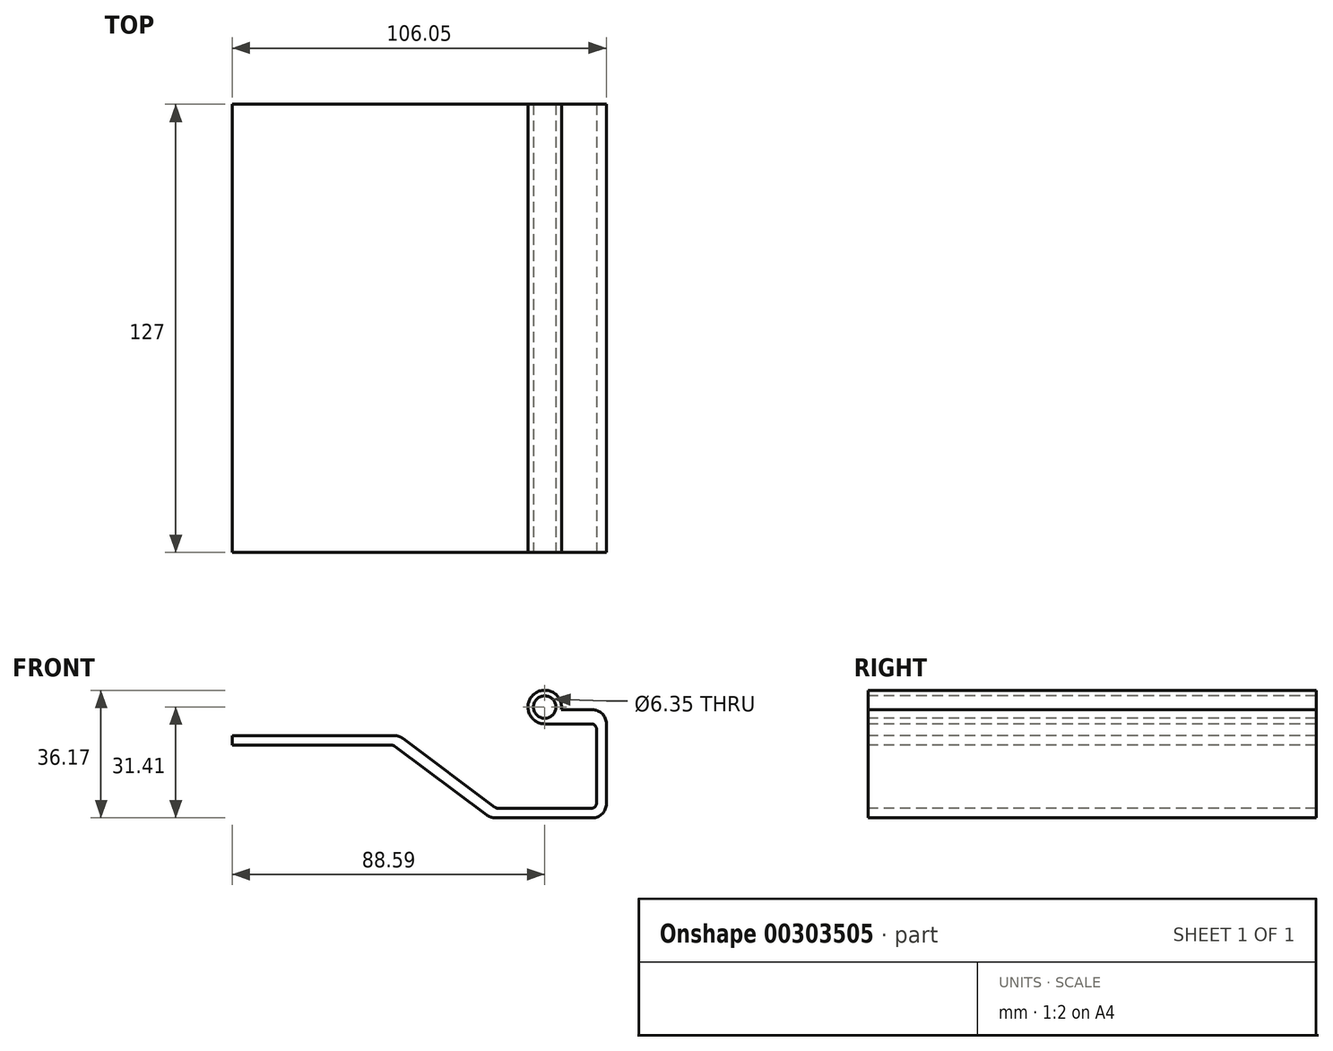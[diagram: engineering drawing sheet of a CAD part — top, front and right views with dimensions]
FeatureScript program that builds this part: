
annotation { "Feature Type Name" : "Feature", "Feature Type Description" : "" }
export const myFeature = defineFeature(function(context is Context, id is Id, definition is map)
    precondition{}
    {
        {
            var Q0;
            Q0=qCreatedBy(makeId("Front.planeOp"),FACE);
            var sketch = newSketch(context, id + "F0", { "sketchPlane" : qUnion([Q0])});
            skCircle(sketch, "E0", {"center": v(0, 0) * mm, "radius": 4.76 * mm});
            skLineSegment(sketch, "E1", {"start": v(0, -4.76) * mm, "end": v(14.67, -4.76) * mm});
            skLineSegment(sketch, "E2", {"start": v(14.67, -4.76) * mm, "end": v(14.67, -28.7) * mm});
            skLineSegment(sketch, "E3", {"start": v(-88.59, -8.13) * mm, "end": v(-88.59, -10.84) * mm});
            skLineSegment(sketch, "E4", {"start": v(17.46, -31.41) * mm, "end": v(17.46, -0.76) * mm});
            skLineSegment(sketch, "E5", {"start": v(17.46, -0.76) * mm, "end": v(4.7, -0.76) * mm});
            skCircle(sketch, "E6", {"center": v(0, 0) * mm, "radius": 3.18 * mm});
            skLineSegment(sketch, "E7", {"start": v(-42.83, -10.84) * mm, "end": v(-15.33, -31.41) * mm});
            skLineSegment(sketch, "E8", {"start": v(-41.19, -8.13) * mm, "end": v(-13.69, -28.7) * mm});
            skLineSegment(sketch, "E9", {"start": v(-88.59, -10.84) * mm, "end": v(-42.83, -10.84) * mm});
            skLineSegment(sketch, "E10", {"start": v(-41.19, -8.13) * mm, "end": v(-88.59, -8.13) * mm});
            skLineSegment(sketch, "E11", {"start": v(-15.33, -31.41) * mm, "end": v(17.46, -31.41) * mm});
            skLineSegment(sketch, "E12", {"start": v(14.67, -28.7) * mm, "end": v(-13.69, -28.7) * mm});
            skSolve(sketch);
        }
        {
            var Q0;
            Q0=makeQuery(id+"F0.imprint","IMPRINT",FACE,{"disambiguationData":[TD([[makeQuery(id+"F0.imprint","IMPRINT",EDGE,{"derivedFrom":sQuery(id+"F0.wireOp",EDGE,"E6")}),-1.0]])]});
            var Q1;
            {var subQ0=sQuery(id+"F0.wireOp",EDGE,"E1");Q1=makeQuery(id+"F0.imprint","IMPRINT",FACE,{"disambiguationData":[TD([[makeQuery(id+"F0.imprint","IMPRINT",EDGE,{"derivedFrom":subQ0}),1.0]])]});}
            extrude(context, id + "F1", {"entities" : qUnion([Q0, Q1]), "oppositeDirection" : true, "depth" : 127 * mm});
        }
        {
            var Q0;
            Q0=makeQuery(id+"F1.opExtrude","SWEPT_EDGE",EDGE,{"disambiguationData":[OSD([sQuery(id+"F0.wireOp",EDGE,"LgDwj1Mh-xzm5-0yFA-xSsm-8yZwKlYHjUQ9"),sQuery(id+"F0.wireOp",EDGE,"sAUc3cFO-EP5O-8lh6-pgeE-BPlsCO7C94gt")])]});
            var Q1;
            Q1=makeQuery(id+"F1.opExtrude","SWEPT_EDGE",EDGE,{"disambiguationData":[OSD([sQuery(id+"F0.wireOp",EDGE,"E4"),sQuery(id+"F0.wireOp",EDGE,"E5")])]});
            var Q2;
            Q2=makeQuery(id+"F1.opExtrude","SWEPT_EDGE",EDGE,{"disambiguationData":[OSD([sQuery(id+"F0.wireOp",EDGE,"yxaHfZF5-8wwv-9skf-2zRC-QGQ34J844eVC"),sQuery(id+"F0.wireOp",EDGE,"Opmgp5wg-7ptp-5E2x-60x0-7ogiDQuXcao6")])]});
            var Q3;
            Q3=makeQuery(id+"F1.opExtrude","SWEPT_EDGE",EDGE,{"disambiguationData":[OSD([sQuery(id+"F0.wireOp",EDGE,"Opmgp5wg-7ptp-5E2x-60x0-7ogiDQuXcao6"),sQuery(id+"F0.wireOp",EDGE,"E4")])]});
            var Q4;
            Q4=makeQuery(id+"F1.opExtrude","SWEPT_EDGE",EDGE,{"disambiguationData":[OSD([sQuery(id+"F0.wireOp",EDGE,"sygippqt-v55u-0h4X-Tq6I-OpJ7BSlTAc0G"),sQuery(id+"F0.wireOp",EDGE,"9sgjengR-0Lgi-cMxs-Qg7z-PEBUjHounaxp")])]});
            var Q5;
            Q5=makeQuery(id+"F1.opExtrude","SWEPT_EDGE",EDGE,{"disambiguationData":[OSD([sQuery(id+"F0.wireOp",EDGE,"Niu9jPIW-rk5n-APbf-PX8w-kWdxQcEE78Rh"),sQuery(id+"F0.wireOp",EDGE,"4ztzvT5v-T6B1-lJR6-r8hH-VqRYV5RCnx5X")])]});
            var Q6;
            Q6=makeQuery(id+"F1.opExtrude","SWEPT_EDGE",EDGE,{"disambiguationData":[OSD([sQuery(id+"F0.wireOp",EDGE,"E7"),sQuery(id+"F0.wireOp",EDGE,"E11")])]});
            var Q7;
            Q7=makeQuery(id+"F1.opExtrude","SWEPT_EDGE",EDGE,{"disambiguationData":[OSD([sQuery(id+"F0.wireOp",EDGE,"E8"),sQuery(id+"F0.wireOp",EDGE,"E10")])]});
            fillet(context, id + "F2", {"entities" : qUnion([Q0, Q1, Q2, Q3, Q4, Q5, Q6, Q7]), "radius" : 3.96 * mm, "tangentPropagation" : true, "allowEdgeOverflow" : false});
        }
        {
            var Q0;
            Q0=makeQuery(id+"F1.opExtrude","SWEPT_EDGE",EDGE,{"disambiguationData":[OSD([sQuery(id+"F0.wireOp",EDGE,"QGqeWTJd-MdKl-cNyP-L5dG-vrMFZphKQkgq"),sQuery(id+"F0.wireOp",EDGE,"LgDwj1Mh-xzm5-0yFA-xSsm-8yZwKlYHjUQ9")])]});
            var Q1;
            Q1=makeQuery(id+"F1.opExtrude","SWEPT_EDGE",EDGE,{"disambiguationData":[OSD([sQuery(id+"F0.wireOp",EDGE,"E2"),sQuery(id+"F0.wireOp",EDGE,"QGqeWTJd-MdKl-cNyP-L5dG-vrMFZphKQkgq")])]});
            var Q2;
            Q2=makeQuery(id+"F1.opExtrude","SWEPT_EDGE",EDGE,{"disambiguationData":[OSD([sQuery(id+"F0.wireOp",EDGE,"E1"),sQuery(id+"F0.wireOp",EDGE,"E2")])]});
            var Q3;
            Q3=makeQuery(id+"F1.opExtrude","SWEPT_EDGE",EDGE,{"disambiguationData":[OSD([sQuery(id+"F0.wireOp",EDGE,"QMmYjeNd-0fDP-D3Gp-oQjs-rBcgyO3WjFIG"),sQuery(id+"F0.wireOp",EDGE,"yxaHfZF5-8wwv-9skf-2zRC-QGQ34J844eVC")])]});
            var Q4;
            Q4=makeQuery(id+"F1.opExtrude","SWEPT_EDGE",EDGE,{"disambiguationData":[OSD([sQuery(id+"F0.wireOp",EDGE,"Niu9jPIW-rk5n-APbf-PX8w-kWdxQcEE78Rh"),sQuery(id+"F0.wireOp",EDGE,"sG2jKDu6-LyPP-gLTV-kqM2-5EQz7XLKZknv")])]});
            var Q5;
            Q5=makeQuery(id+"F1.opExtrude","SWEPT_EDGE",EDGE,{"disambiguationData":[OSD([sQuery(id+"F0.wireOp",EDGE,"E8"),sQuery(id+"F0.wireOp",EDGE,"E12")])]});
            var Q6;
            Q6=makeQuery(id+"F1.opExtrude","SWEPT_EDGE",EDGE,{"disambiguationData":[OSD([sQuery(id+"F0.wireOp",EDGE,"E7"),sQuery(id+"F0.wireOp",EDGE,"E9")])]});
            fillet(context, id + "F3", {"entities" : qUnion([Q0, Q1, Q2, Q3, Q4, Q5, Q6]), "radius" : 1.52 * mm, "tangentPropagation" : true, "allowEdgeOverflow" : false});
        }
    });
